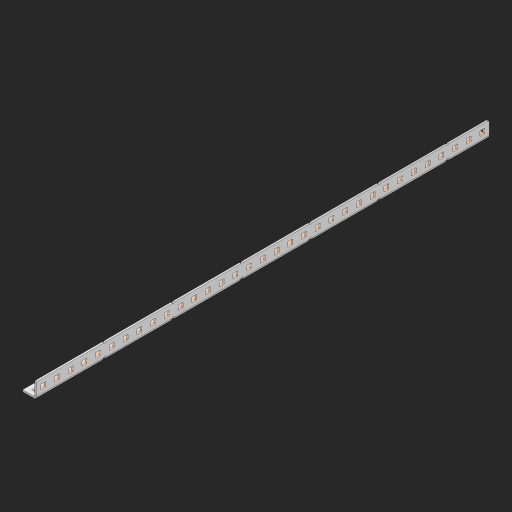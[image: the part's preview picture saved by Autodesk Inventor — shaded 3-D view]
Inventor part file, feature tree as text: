
AUTODESK INVENTOR PART (.ipt)
format: ipt  version: 2023 (Build 270158000, 158)  size: 1,331,200 bytes
history: native  units: in
note: dims shown in document units (in); Inventor stores cm internally (conversion verified against a paired STEP export)
features: other x247, extrude x97, sheet_metal_op x11, sketch x10, pattern_linear x2, mirror x1, chamfer x1
ambient origin geometry x8: Origin, YZ Plane, XZ Plane, XY Plane, X Axis, Y Axis, Z Axis, Center Point
bodies: Solid1 (feature_tree), Body (feature_tree)
feature tree (369):
  other  "Alu Half C 1x2x1x33"
  other  "Table"
  other  "Alu C 1x2x1x35"
  other  "Alu C 1x2x1x34"
  other  "Alu C 1x2x1x33"
  other  "Alu C 1x2x1x32"
  other  "Alu C 1x2x1x31"
  other  "Alu C 1x2x1x30"
  other  "Alu C 1x2x1x29"
  other  "Alu C 1x2x1x28"
  other  "Alu C 1x2x1x27"
  other  "Alu C 1x2x1x26"
  other  "Alu C 1x2x1x25"
  other  "Alu C 1x2x1x24"
  other  "Alu C 1x2x1x23"
  other  "Alu C 1x2x1x22"
  other  "Alu C 1x2x1x21"
  other  "Alu C 1x2x1x20"
  other  "Alu C 1x2x1x19"
  other  "Alu C 1x2x1x18"
  other  "Alu C 1x2x1x17"
  other  "Alu C 1x2x1x16"
  other  "Alu C 1x2x1x15"
  other  "Alu C 1x2x1x14"
  other  "Alu C 1x2x1x13"
  other  "Alu C 1x2x1x12"
  other  "Alu C 1x2x1x11"
  other  "Alu C 1x2x1x10"
  other  "Alu C 1x2x1x9"
  other  "Alu C 1x2x1x8"
  other  "Alu C 1x2x1x7"
  other  "Alu C 1x2x1x6"
  other  "Alu C 1x2x1x5"
  other  "Alu C 1x2x1x4"
  other  "Alu C 1x2x1x3"
  other  "Alu C 1x2x1x2"
  other  "Alu C 1x2x1x1"
  other  "Steel C 1x2x1x35"
  other  "Steel C 1x2x1x34"
  other  "Steel C 1x2x1x33"
  other  "Steel C 1x2x1x32"
  other  "Steel C 1x2x1x31"
  other  "Steel C 1x2x1x30"
  other  "Steel C 1x2x1x29"
  other  "Steel C 1x2x1x28"
  other  "Steel C 1x2x1x27"
  other  "Steel C 1x2x1x26"
  other  "Steel C 1x2x1x25"
  other  "Steel C 1x2x1x24"
  other  "Steel C 1x2x1x23"
  other  "Steel C 1x2x1x22"
  other  "Steel C 1x2x1x21"
  other  "Steel C 1x2x1x20"
  other  "Steel C 1x2x1x19"
  other  "Steel C 1x2x1x18"
  other  "Steel C 1x2x1x17"
  other  "Steel C 1x2x1x16"
  other  "Steel C 1x2x1x15"
  other  "Steel C 1x2x1x14"
  other  "Steel C 1x2x1x13"
  other  "Steel C 1x2x1x12"
  other  "Steel C 1x2x1x11"
  other  "Steel C 1x2x1x10"
  other  "Steel C 1x2x1x9"
  other  "Steel C 1x2x1x8"
  other  "Steel C 1x2x1x7"
  other  "Steel C 1x2x1x6"
  other  "Steel C 1x2x1x5"
  other  "Steel C 1x2x1x4"
  other  "Steel C 1x2x1x3"
  other  "Steel C 1x2x1x2"
  other  "Steel C 1x2x1x1"
  other  "Alu Half C 1x2x1x35"
  other  "Alu Half C 1x2x1x34"
  other  "Alu Half C 1x2x1x32"
  other  "Alu Half C 1x2x1x31"
  other  "Alu Half C 1x2x1x30"
  other  "Alu Half C 1x2x1x29"
  other  "Alu Half C 1x2x1x28"
  other  "Alu Half C 1x2x1x27"
  other  "Alu Half C 1x2x1x26"
  other  "Alu Half C 1x2x1x25"
  other  "Alu Half C 1x2x1x24"
  other  "Alu Half C 1x2x1x23"
  other  "Alu Half C 1x2x1x22"
  other  "Alu Half C 1x2x1x21"
  other  "Alu Half C 1x2x1x20"
  other  "Alu Half C 1x2x1x19"
  other  "Alu Half C 1x2x1x18"
  other  "Alu Half C 1x2x1x17"
  other  "Alu Half C 1x2x1x16"
  other  "Alu Half C 1x2x1x15"
  other  "Alu Half C 1x2x1x14"
  other  "Alu Half C 1x2x1x13"
  other  "Alu Half C 1x2x1x12"
  other  "Alu Half C 1x2x1x11"
  other  "Alu Half C 1x2x1x10"
  other  "Alu Half C 1x2x1x9"
  other  "Alu Half C 1x2x1x8"
  other  "Alu Half C 1x2x1x7"
  other  "Alu Half C 1x2x1x6"
  other  "Alu Half C 1x2x1x5"
  other  "Alu Half C 1x2x1x4"
  other  "Alu Half C 1x2x1x3"
  other  "Alu Half C 1x2x1x2"
  other  "Alu Half C 1x2x1x1"
  other  "Steel Half C 1x2x1x35"
  other  "Steel Half C 1x2x1x34"
  other  "Steel Half C 1x2x1x33"
  other  "Steel Half C 1x2x1x32"
  other  "Steel Half C 1x2x1x31"
  other  "Steel Half C 1x2x1x30"
  other  "Steel Half C 1x2x1x29"
  other  "Steel Half C 1x2x1x28"
  other  "Steel Half C 1x2x1x27"
  other  "Steel Half C 1x2x1x26"
  other  "Steel Half C 1x2x1x25"
  other  "Steel Half C 1x2x1x24"
  other  "Steel Half C 1x2x1x23"
  other  "Steel Half C 1x2x1x22"
  other  "Steel Half C 1x2x1x21"
  other  "Steel Half C 1x2x1x20"
  other  "Steel Half C 1x2x1x19"
  other  "Steel Half C 1x2x1x18"
  other  "Steel Half C 1x2x1x17"
  other  "Steel Half C 1x2x1x16"
  other  "Steel Half C 1x2x1x15"
  other  "Steel Half C 1x2x1x14"
  other  "Steel Half C 1x2x1x13"
  other  "Steel Half C 1x2x1x12"
  other  "Steel Half C 1x2x1x11"
  other  "Steel Half C 1x2x1x10"
  other  "Steel Half C 1x2x1x9"
  other  "Steel Half C 1x2x1x8"
  other  "Steel Half C 1x2x1x7"
  other  "Steel Half C 1x2x1x6"
  other  "Steel Half C 1x2x1x5"
  other  "Steel Half C 1x2x1x4"
  other  "Steel Half C 1x2x1x3"
  other  "Steel Half C 1x2x1x2"
  other  "Steel Half C 1x2x1x1"
  sheet_metal_op  "Flanges"
  other  "Flange Pattern Plane"
  other  "Flange Pattern Sketch"
  sheet_metal_op  "Flange Pattern"
  sheet_metal_op  "Body Pattern"
  pattern_linear  "Center Pattern"  Spacing1=0.0625in  [1 undecoded]
  other  "Arc Length"
  mirror  "Notch Mirror"
  pattern_linear  "Notch Pattern"  Spacing1=0.182in  [1 undecoded]
  chamfer  "End Chamfer"
  extrude  "Half Cut"  Depth=0.02in
  sketch  "Sketch1"  dims[d0=1.0in]
  other  "Plate1"
  sketch  "Sketch2"  dims[d1=16.5in]
  other  "Plate2"
  sheet_metal_op  "Bend1"
  sheet_metal_op  "Corner1"
  sketch  "Sketch3"  dims[d2=0.0625in]
  sketch  "Sketch7"  dims[d3=0.0625in]
  other  "Srf1"
  other  "Srf2"
  sketch  "Sketch8"  dims[d4=0.0312in]
  sketch  "Sketch9"  dims[d5=0.125in]
  other  "Srf91"
  sheet_metal_op  "Body Pattern Sketch"
  other  "Srf92"
  sketch  "Sketch13"  dims[d6=0.0625in]
  sketch  "Sketch14"  dims[d7=0.5in d8=90.0deg d9=0.0312in]
  sketch  "Sketch15"  dims[d10=0.25in]
  sketch  "Sketch16"  dims[d11=0.0625in d12=0.0625in d16=0.182in d17=0.02in d18=0.0625in d19=0.0in d20=0.25in d21=0.25in d38=12.9921in d40=0.5in d41=0.3937in d43=1.0in d46=0.172in d47=1.0in d48=0.0in d49=0.182in d50=0.02in d51=0.25in d52=0.25in d53=0.0625in d54=0.0in d55=0.172in d56=1.0in d57=0.0in d58=0.25in d60=12.9921in d62=0.5in d63=0.3937in d65=0.5in d85=0.1473in d86=0.1782in d88=0.04in d89=0.0625in d90=0.0in d91=0.04in d92=0.0491in d95=2.5in d96=0.04in d97=0.25in d98=45.0deg d99=0.25in d100=0.5in d101=0.0in d102=2.497in d106=0.182in d107=0.02in d108=0.5in d109=0.5in d110=0.0625in d111=0.0in d112=0.172in d113=0.5in d114=0.0in d117=0.5in d118=0.5in d119=0.5in]
  other  "Srf786"
  other  "Srf823"
  other  "Srf824"
  other  "Srf825"
  other  "Srf826"
  other  "Srf827"
  other  "Srf828"
  other  "Srf829"
  other  "Srf856"
  other  "Srf857"
  other  "Srf858"
  other  "Srf859"
  other  "Srf860"
  other  "Srf861"
  other  "Srf862"
  other  "Srf889"
  other  "Srf890"
  other  "Srf891"
  other  "Srf892"
  other  "Srf893"
  other  "Srf894"
  other  "Srf895"
  other  "Srf896"
  other  "Srf922"
  other  "Srf923"
  other  "Srf924"
  other  "Srf925"
  other  "Srf926"
  other  "Srf959"
  other  "Srf960"
  other  "Srf961"
  other  "Srf962"
  other  "Srf963"
  other  "Srf996"
  other  "Srf997"
  other  "Srf998"
  other  "Srf999"
  other  "Srf1000"
  other  "Srf1143"
  other  "Srf1144"
  other  "Srf1145"
  other  "Srf1146"
  other  "Srf1147"
  other  "Srf1148"
  other  "Srf1149"
  other  "Srf1150"
  other  "Srf1151"
  other  "Srf1152"
  other  "Srf1153"
  other  "Srf1154"
  other  "Srf1155"
  other  "Srf1156"
  other  "Srf1157"
  other  "Srf1158"
  other  "Srf1159"
  other  "Srf1160"
  other  "Srf1161"
  other  "Srf1199"
  other  "Srf1200"
  other  "Srf1201"
  other  "Srf1202"
  other  "Srf1203"
  other  "Srf1204"
  other  "Srf1205"
  other  "Srf1206"
  other  "Srf1207"
  other  "Srf1208"
  other  "Srf1209"
  other  "Srf1210"
  other  "Srf1211"
  other  "Srf1212"
  other  "Srf1213"
  other  "Srf1214"
  other  "Srf1215"
  other  "Srf1216"
  other  "Srf1217"
  other  "Srf1255"
  other  "Srf1256"
  other  "Srf1257"
  other  "Srf1258"
  other  "Srf1259"
  other  "Srf1260"
  other  "Srf1261"
  other  "Srf1262"
  other  "Srf1263"
  other  "Srf1264"
  other  "Srf1265"
  other  "Srf1266"
  other  "Srf1267"
  other  "Srf1268"
  other  "Srf1269"
  other  "Srf1270"
  other  "Srf1271"
  other  "Srf1272"
  other  "Srf1273"
  sheet_metal_op  "Flange Stamp"
  sheet_metal_op  "Flange Circle"
  sheet_metal_op  "Body Stamp"
  sheet_metal_op  "Body Circle"
  other  "Center Stamp"
  other  "Center Circle"
  sheet_metal_op  "Notch"
  extrude  "ExtrusionSrf2"  Depth=0.0625in
  extrude  "ExtrusionSrf92"  TaperAngle=0.0deg  [1 undecoded]
  extrude  "ExtrusionSrf823"  Depth=0.5in
  extrude  "ExtrusionSrf824"  Depth=0.5in
  extrude  "ExtrusionSrf825"  Depth=0.5in
  extrude  "ExtrusionSrf826"  Depth=0.5in
  extrude  "ExtrusionSrf827"  Depth=1.0in TaperAngle=0.0deg
  extrude  "ExtrusionSrf828"  Depth=0.182in
  extrude  "ExtrusionSrf829"  Depth=0.02in
  extrude  "ExtrusionSrf856"  Depth=0.5in
  extrude  "ExtrusionSrf857"  Depth=0.5in
  extrude  "ExtrusionSrf858"  Depth=0.0625in
  extrude  "ExtrusionSrf859"  TaperAngle=0.0deg  [1 undecoded]
  extrude  "ExtrusionSrf860"  Depth=0.5in
  extrude  "ExtrusionSrf861"  Depth=1.0in TaperAngle=0.0deg
  extrude  "ExtrusionSrf862"  Depth=0.5in
  extrude  "ExtrusionSrf889"  Depth=0.5in
  extrude  "ExtrusionSrf890"  Depth=0.5in
  extrude  "ExtrusionSrf891"  Depth=0.5in
  extrude  "ExtrusionSrf892"  Depth=0.5in
  extrude  "ExtrusionSrf893"  Depth=0.5in
  extrude  "ExtrusionSrf894"  Depth=0.0625in
  extrude  "ExtrusionSrf895"  TaperAngle=0.0deg  [1 undecoded]
  extrude  "ExtrusionSrf896"  Depth=0.5in
  extrude  "ExtrusionSrf922"  Depth=0.5in
  extrude  "ExtrusionSrf923"  Depth=0.5in
  extrude  "ExtrusionSrf924"  Depth=0.5in TaperAngle=45.0deg
  extrude  "ExtrusionSrf925"  Depth=0.5in
  extrude  "ExtrusionSrf926"  Depth=0.5in TaperAngle=0.0deg
  extrude  "ExtrusionSrf959"  Depth=0.5in
  extrude  "ExtrusionSrf960"  Depth=0.182in
  extrude  "ExtrusionSrf961"  Depth=0.02in
  extrude  "ExtrusionSrf962"  Depth=0.5in
  extrude  "ExtrusionSrf963"  Depth=0.5in
  extrude  "ExtrusionSrf996"  Depth=0.0625in
  extrude  "ExtrusionSrf997"  TaperAngle=0.0deg  [1 undecoded]
  extrude  "ExtrusionSrf998"  Depth=0.5in
  extrude  "ExtrusionSrf999"  Depth=0.5in TaperAngle=0.0deg
  extrude  "ExtrusionSrf1000"  Depth=0.5in
  extrude  "ExtrusionSrf1143"  Depth=0.5in
  extrude  "ExtrusionSrf1144"  Depth=0.5in
  extrude  "ExtrusionSrf1145"  [1 undecoded]
  extrude  "ExtrusionSrf1146"  [1 undecoded]
  extrude  "ExtrusionSrf1147"  [1 undecoded]
  extrude  "ExtrusionSrf1148"  [1 undecoded]
  extrude  "ExtrusionSrf1149"  [1 undecoded]
  extrude  "ExtrusionSrf1150"  [1 undecoded]
  extrude  "ExtrusionSrf1151"  [1 undecoded]
  extrude  "ExtrusionSrf1152"  [1 undecoded]
  extrude  "ExtrusionSrf1153"  [1 undecoded]
  extrude  "ExtrusionSrf1154"  [1 undecoded]
  extrude  "ExtrusionSrf1155"  [1 undecoded]
  extrude  "ExtrusionSrf1156"  [1 undecoded]
  extrude  "ExtrusionSrf1157"  [1 undecoded]
  extrude  "ExtrusionSrf1158"  [1 undecoded]
  extrude  "ExtrusionSrf1159"  [1 undecoded]
  extrude  "ExtrusionSrf1160"  [1 undecoded]
  extrude  "ExtrusionSrf1161"  [1 undecoded]
  extrude  "ExtrusionSrf1199"  [1 undecoded]
  extrude  "ExtrusionSrf1200"  [1 undecoded]
  extrude  "ExtrusionSrf1201"  [1 undecoded]
  extrude  "ExtrusionSrf1202"  [1 undecoded]
  extrude  "ExtrusionSrf1203"  [1 undecoded]
  extrude  "ExtrusionSrf1204"  [1 undecoded]
  extrude  "ExtrusionSrf1205"  [1 undecoded]
  extrude  "ExtrusionSrf1206"  [1 undecoded]
  extrude  "ExtrusionSrf1207"  [1 undecoded]
  extrude  "ExtrusionSrf1208"  [1 undecoded]
  extrude  "ExtrusionSrf1209"  [1 undecoded]
  extrude  "ExtrusionSrf1210"  [1 undecoded]
  extrude  "ExtrusionSrf1211"  [1 undecoded]
  extrude  "ExtrusionSrf1212"  [1 undecoded]
  extrude  "ExtrusionSrf1213"  [1 undecoded]
  extrude  "ExtrusionSrf1214"  [1 undecoded]
  extrude  "ExtrusionSrf1215"  [1 undecoded]
  extrude  "ExtrusionSrf1216"  [1 undecoded]
  extrude  "ExtrusionSrf1217"  [1 undecoded]
  extrude  "ExtrusionSrf1255"  [1 undecoded]
  extrude  "ExtrusionSrf1256"  [1 undecoded]
  extrude  "ExtrusionSrf1257"  [1 undecoded]
  extrude  "ExtrusionSrf1258"  [1 undecoded]
  extrude  "ExtrusionSrf1259"  [1 undecoded]
  extrude  "ExtrusionSrf1260"  [1 undecoded]
  extrude  "ExtrusionSrf1261"  [1 undecoded]
  extrude  "ExtrusionSrf1262"  [1 undecoded]
  extrude  "ExtrusionSrf1263"  [1 undecoded]
  extrude  "ExtrusionSrf1264"  [1 undecoded]
  extrude  "ExtrusionSrf1265"  [1 undecoded]
  extrude  "ExtrusionSrf1266"  [1 undecoded]
  extrude  "ExtrusionSrf1267"  [1 undecoded]
  extrude  "ExtrusionSrf1268"  [1 undecoded]
  extrude  "ExtrusionSrf1269"  [1 undecoded]
  extrude  "ExtrusionSrf1270"  [1 undecoded]
  extrude  "ExtrusionSrf1271"  [1 undecoded]
  extrude  "ExtrusionSrf1272"  [1 undecoded]
  extrude  "ExtrusionSrf1273"  [1 undecoded]
note: 61 required parameter values undecoded (feature->parameter linkage not recoverable at this tier; creation-order binding heuristic only, values carry confidence <= 0.55)
